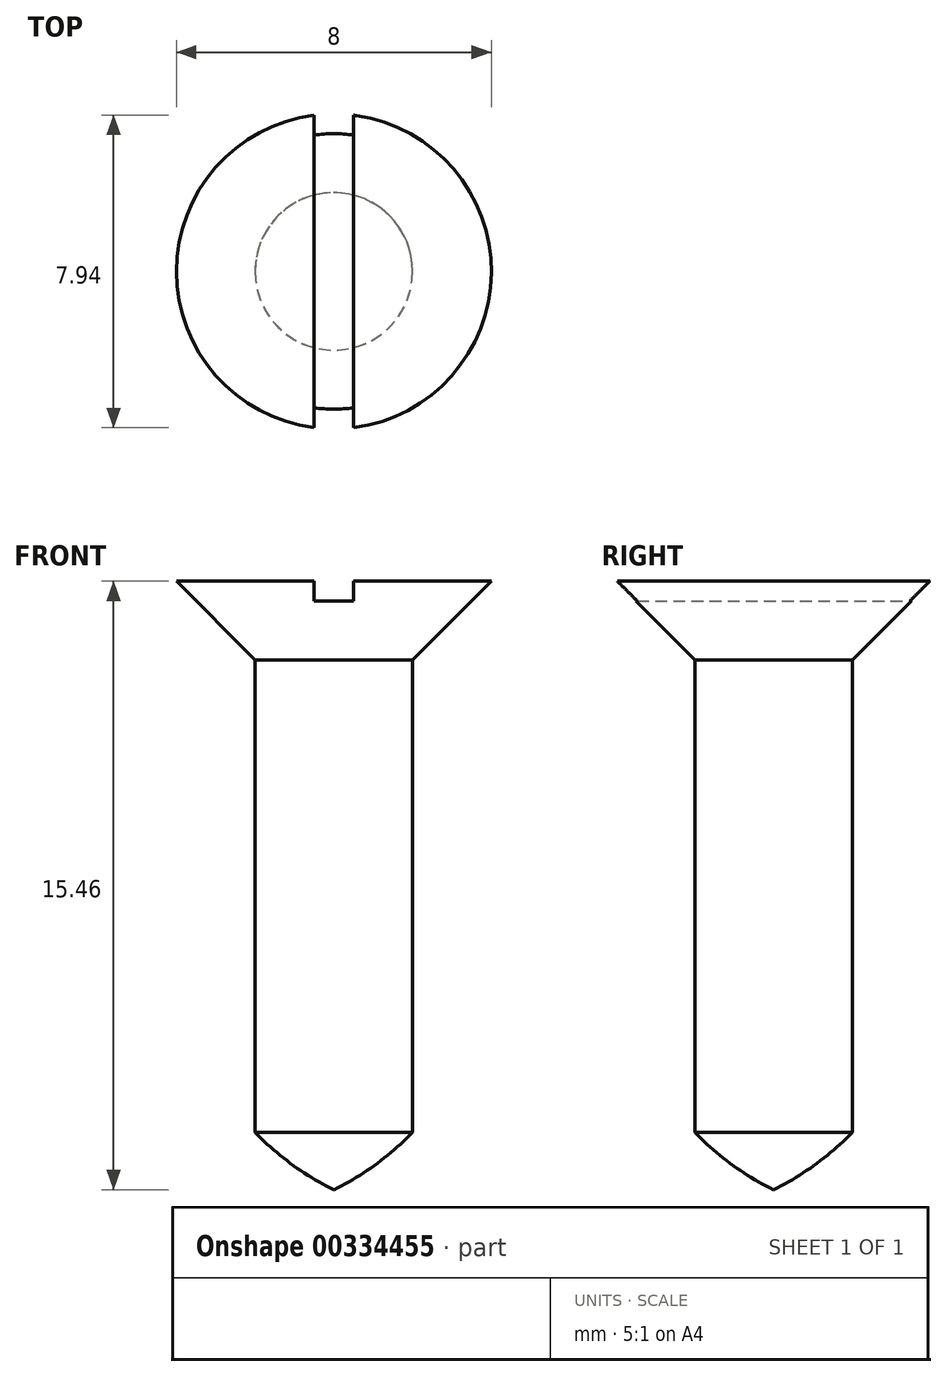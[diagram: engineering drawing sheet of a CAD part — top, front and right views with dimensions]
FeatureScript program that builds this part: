
annotation { "Feature Type Name" : "Feature", "Feature Type Description" : "" }
export const myFeature = defineFeature(function(context is Context, id is Id, definition is map)
    precondition{}
    {
        {
            var Q0;
            Q0=qCreatedBy(makeId("Front.planeOp"),FACE);
            var sketch = newSketch(context, id + "F0", { "sketchPlane" : qUnion([Q0])});
            skLineSegment(sketch, "E0", {"start": v(0, 0) * mm, "end": v(0, 14) * mm});
            skLineSegment(sketch, "E1", {"start": v(0, 14) * mm, "end": v(4, 14) * mm});
            skLineSegment(sketch, "E2", {"start": v(4, 14) * mm, "end": v(2, 12) * mm});
            skLineSegment(sketch, "E3", {"start": v(2, 12) * mm, "end": v(2, 0) * mm});
            skArc(sketch, "E4", {"start": v(0, -1.46) * mm, "mid": v(1.06, -0.82) * mm, "end": v(2, 0) * mm});
            skLineSegment(sketch, "E5", {"start": v(0, -1.46) * mm, "end": v(0, 0) * mm});
            skSolve(sketch);
        }
        {
            var Q0;
            Q0=makeQuery(id+"F0.imprint","IMPRINT",FACE,{"disambiguationData":[TD([[makeQuery(id+"F0.imprint","IMPRINT",EDGE,{"derivedFrom":sQuery(id+"F0.wireOp",EDGE,"E0")}),-1.0]])]});
            var Q1;
            Q1=sQuery(id+"F0.wireOp",EDGE,"E0");
            revolve(context, id + "F1", {"entities" : qUnion([Q0]), "axis" : qUnion([Q1]), "revolveType" : RevolveType.FULL});
        }
        {
            var Q0;
            Q0=makeQuery(id+"F1.opRevolve","SWEPT_FACE",FACE,{"disambiguationData":[OSD([sQuery(id+"F0.wireOp",EDGE,"E1")])]});
            var sketch = newSketch(context, id + "F2", { "sketchPlane" : qUnion([Q0])});
            skLineSegment(sketch, "E6.bottom", {"start": v(-0.5, -5) * mm, "end": v(0.5, -5) * mm});
            skLineSegment(sketch, "E6.top", {"start": v(-0.5, 5) * mm, "end": v(0.5, 5) * mm});
            skLineSegment(sketch, "E6.left", {"start": v(-0.5, -5) * mm, "end": v(-0.5, 5) * mm});
            skLineSegment(sketch, "E6.right", {"start": v(0.5, -5) * mm, "end": v(0.5, 5) * mm});
            skPoint(sketch, "E6.middle", {"position": v(0, 0) * mm});
            skSolve(sketch);
        }
        {
            var Q0;
            {var subQ0=sQuery(id+"F2.wireOp",EDGE,"E6.left");var subQ1=makeQuery(id+"F1.opRevolve","SWEPT_EDGE",EDGE,{"disambiguationData":[OSD([sQuery(id+"F0.wireOp",EDGE,"E1"),sQuery(id+"F0.wireOp",EDGE,"E2")])]});var subQ2=makeQuery(id+"F2.imprint","INTERSECT",VERTEX,{"disambiguationData":[OD(0.0)],"derivedFrom":[subQ1,subQ0]});Q0=makeQuery(id+"F2.imprint","IMPRINT",FACE,{"disambiguationData":[TD([[makeQuery(id+"F2.imprint","IMPRINT",EDGE,{"disambiguationData":[TD([[subQ2,-1.0]])],"derivedFrom":subQ0}),-1.0]])]});}
            extrude(context, id + "F3", {"entities" : qUnion([Q0]), "operationType" : NewBodyOperationType.REMOVE, "oppositeDirection" : true, "depth" : 0.5 * mm});
        }
    });
